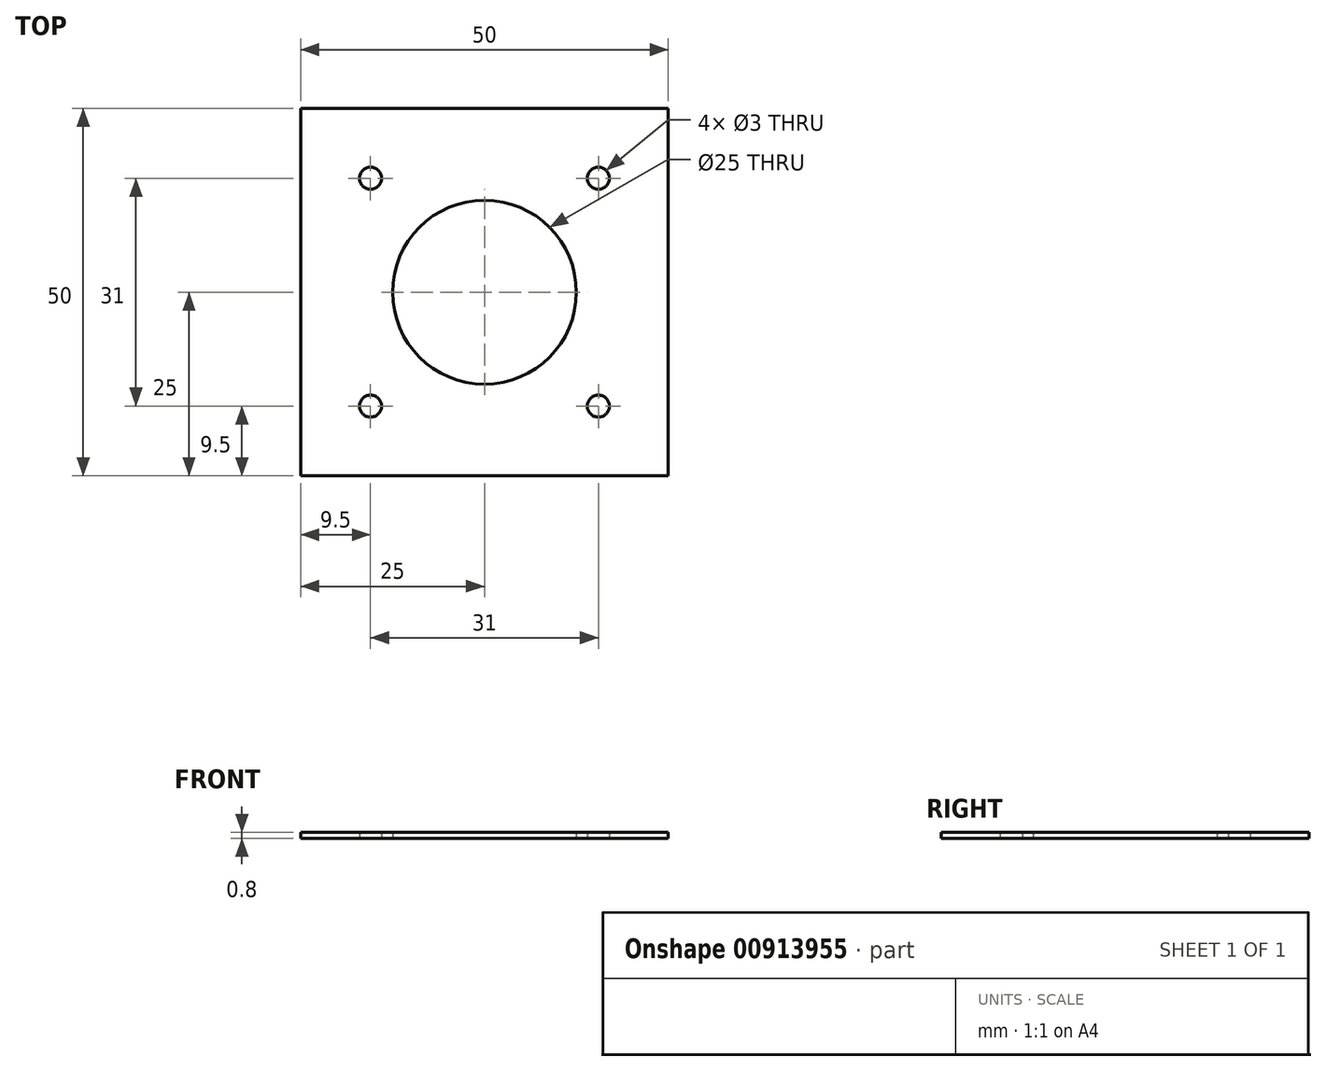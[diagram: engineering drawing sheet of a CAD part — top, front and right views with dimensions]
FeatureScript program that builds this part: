
annotation { "Feature Type Name" : "Feature", "Feature Type Description" : "" }
export const myFeature = defineFeature(function(context is Context, id is Id, definition is map)
    precondition{}
    {
        {
            var Q0;
            Q0=qCreatedBy(makeId("Top.planeOp"),FACE);
            var sketch = newSketch(context, id + "F0", { "sketchPlane" : qUnion([Q0])});
            skLineSegment(sketch, "E0.bottom", {"start": v(-25, 25) * mm, "end": v(25, 25) * mm});
            skLineSegment(sketch, "E0.top", {"start": v(-25, -25) * mm, "end": v(25, -25) * mm});
            skLineSegment(sketch, "E0.left", {"start": v(-25, 25) * mm, "end": v(-25, -25) * mm});
            skLineSegment(sketch, "E0.right", {"start": v(25, 25) * mm, "end": v(25, -25) * mm});
            skPoint(sketch, "E0.middle", {"position": v(0, 0) * mm});
            skCircle(sketch, "E1", {"center": v(0, 0) * mm, "radius": 12.5 * mm});
            skLineSegment(sketch, "E2.bottom", {"start": v(15.5, 15.5) * mm, "end": v(-15.5, 15.5) * mm, "construction": true});
            skLineSegment(sketch, "E2.top", {"start": v(15.5, -15.5) * mm, "end": v(-15.5, -15.5) * mm, "construction": true});
            skLineSegment(sketch, "E2.left", {"start": v(15.5, 15.5) * mm, "end": v(15.5, -15.5) * mm, "construction": true});
            skLineSegment(sketch, "E2.right", {"start": v(-15.5, 15.5) * mm, "end": v(-15.5, -15.5) * mm, "construction": true});
            skCircle(sketch, "E3", {"center": v(15.5, 15.5) * mm, "radius": 1.5 * mm});
            skCircle(sketch, "E4.1.0", {"center": v(-15.5, 15.5) * mm, "radius": 1.5 * mm});
            skCircle(sketch, "E4.2.0", {"center": v(-15.5, -15.5) * mm, "radius": 1.5 * mm});
            skCircle(sketch, "E4.3.0", {"center": v(15.5, -15.5) * mm, "radius": 1.5 * mm});
            skSolve(sketch);
        }
        {
            var Q0;
            Q0=makeQuery(id+"F0.imprint","IMPRINT",FACE,{"disambiguationData":[TD([[makeQuery(id+"F0.imprint","IMPRINT",EDGE,{"derivedFrom":sQuery(id+"F0.wireOp",EDGE,"E0.bottom")}),-1.0]])]});
            extrude(context, id + "F1", {"entities" : qUnion([Q0]), "depth" : 0.8 * mm, "offsetDistance" : 25 * mm});
        }
    });
